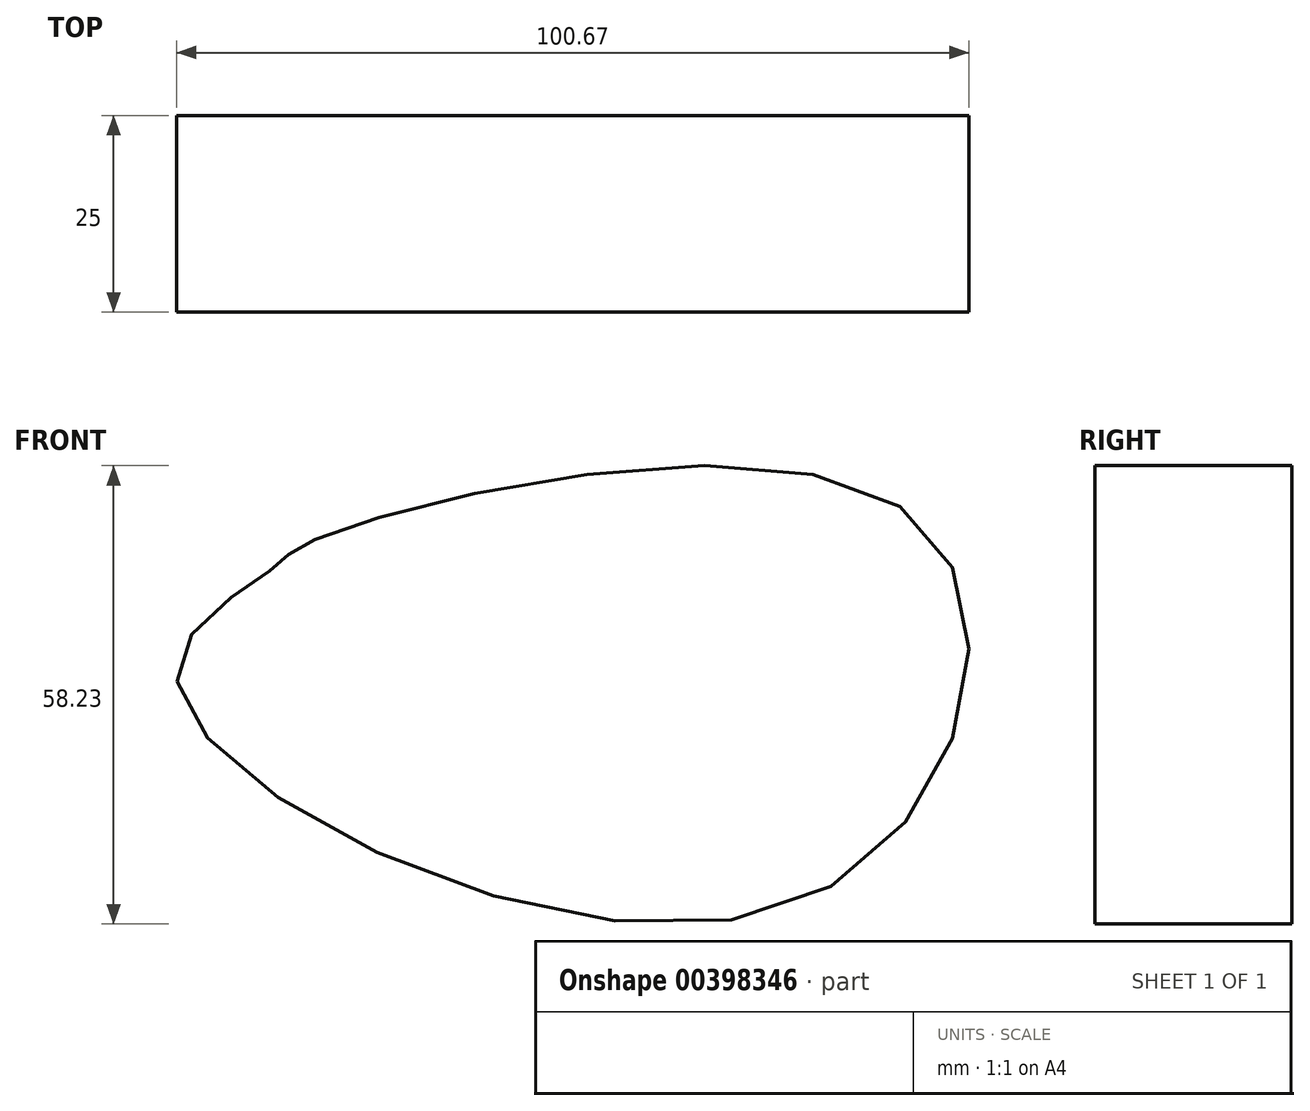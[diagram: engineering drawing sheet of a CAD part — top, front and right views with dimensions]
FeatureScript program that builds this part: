
annotation { "Feature Type Name" : "Feature", "Feature Type Description" : "" }
export const myFeature = defineFeature(function(context is Context, id is Id, definition is map)
    precondition{}
    {
        {
            var Q0;
            Q0=qCreatedBy(makeId("Front.planeOp"),FACE);
            var sketch = newSketch(context, id + "F0", { "sketchPlane" : qUnion([Q0])});
            skFitSpline(sketch, "E0", {"points": [v(-57.55, 47.04) * mm, v(20.87, 18.78) * mm, v(36.02, 67.97) * mm, v(-40.71, 64.81) * mm, v(-45.23, 61.46) * mm, v(-57.55, 47.04) * mm]});
            skSolve(sketch);
        }
        {
            var Q0;
            Q0 = qSketchRegion(id + "F0", true);
            extrude(context, id + "F1", {"entities" : qUnion([Q0]), "depth" : 25 * mm});
        }
    });
